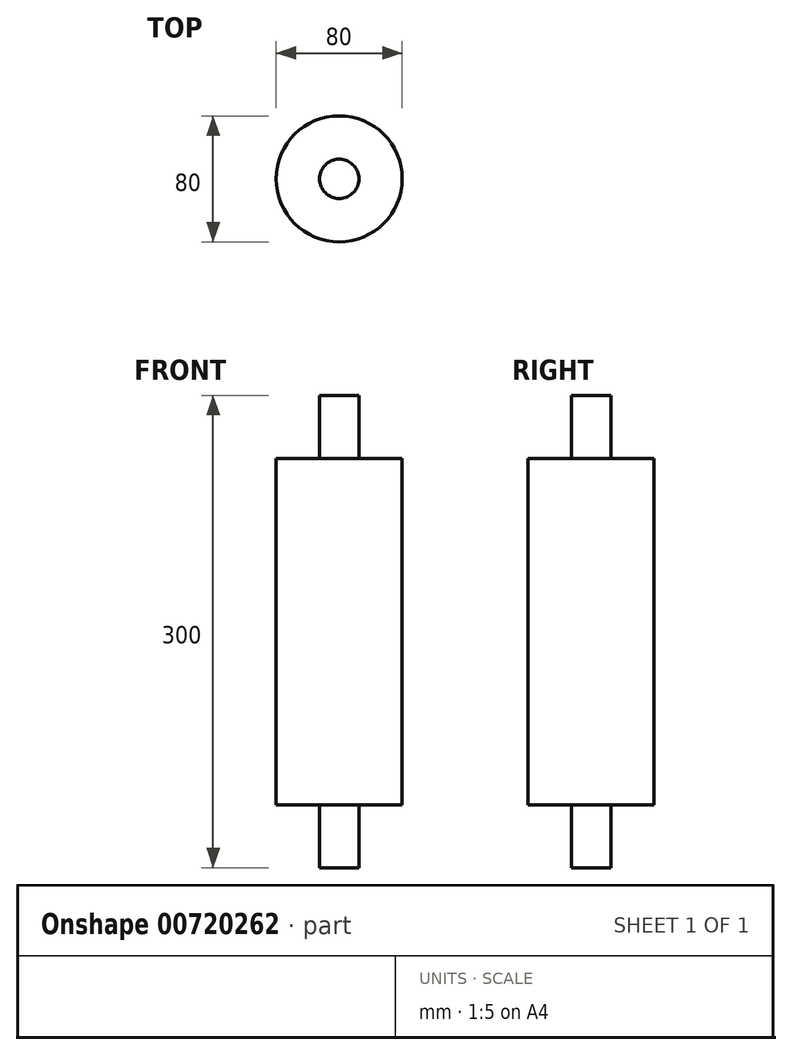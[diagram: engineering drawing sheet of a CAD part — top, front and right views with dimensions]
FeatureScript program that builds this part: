
annotation { "Feature Type Name" : "Feature", "Feature Type Description" : "" }
export const myFeature = defineFeature(function(context is Context, id is Id, definition is map)
    precondition{}
    {
        {
            var Q0;
            Q0=qCreatedBy(makeId("Top.planeOp"),FACE);
            var sketch = newSketch(context, id + "F0", { "sketchPlane" : qUnion([Q0])});
            skCircle(sketch, "E0", {"center": v(0, 0) * mm, "radius": 40 * mm});
            skSolve(sketch);
        }
        {
            var Q0;
            Q0=makeQuery(id+"F0.imprint","IMPRINT",FACE,{"disambiguationData":[TD([[makeQuery(id+"F0.imprint","IMPRINT",EDGE,{"derivedFrom":sQuery(id+"F0.wireOp",EDGE,"E0")}),1.0]])]});
            extrude(context, id + "F1", {"entities" : qUnion([Q0]), "depth" : 220 * mm, "offsetDistance" : 25 * mm});
        }
        {
            var Q0;
            Q0=makeQuery(id+"F1.opExtrude","CAP_FACE",FACE,{"disambiguationData":[OSD([sQuery(id+"F0.wireOp",EDGE,"E0")])],"isStart":true});
            var sketch = newSketch(context, id + "F2", { "sketchPlane" : qUnion([Q0])});
            skCircle(sketch, "E1", {"center": v(0, 0) * mm, "radius": 12.5 * mm});
            skSolve(sketch);
        }
        {
            var Q0;
            Q0=makeQuery(id+"F2.imprint","IMPRINT",FACE,{"disambiguationData":[TD([[makeQuery(id+"F2.imprint","IMPRINT",EDGE,{"derivedFrom":sQuery(id+"F2.wireOp",EDGE,"E1")}),1.0]])]});
            extrude(context, id + "F3", {"entities" : qUnion([Q0]), "operationType" : NewBodyOperationType.ADD, "depth" : 40 * mm, "offsetDistance" : 25 * mm});
        }
        {
            var Q0;
            Q0=makeQuery(id+"F1.opExtrude","CAP_FACE",FACE,{"disambiguationData":[OSD([sQuery(id+"F0.wireOp",EDGE,"E0")])],"isStart":false});
            var sketch = newSketch(context, id + "F4", { "sketchPlane" : qUnion([Q0])});
            skCircle(sketch, "E2", {"center": v(0, 0) * mm, "radius": 12.5 * mm});
            skSolve(sketch);
        }
        {
            var Q0;
            Q0=makeQuery(id+"F4.imprint","IMPRINT",FACE,{"disambiguationData":[TD([[makeQuery(id+"F4.imprint","IMPRINT",EDGE,{"derivedFrom":sQuery(id+"F4.wireOp",EDGE,"E2")}),1.0]])]});
            extrude(context, id + "F5", {"entities" : qUnion([Q0]), "operationType" : NewBodyOperationType.ADD, "depth" : 40 * mm, "offsetDistance" : 25 * mm});
        }
    });
